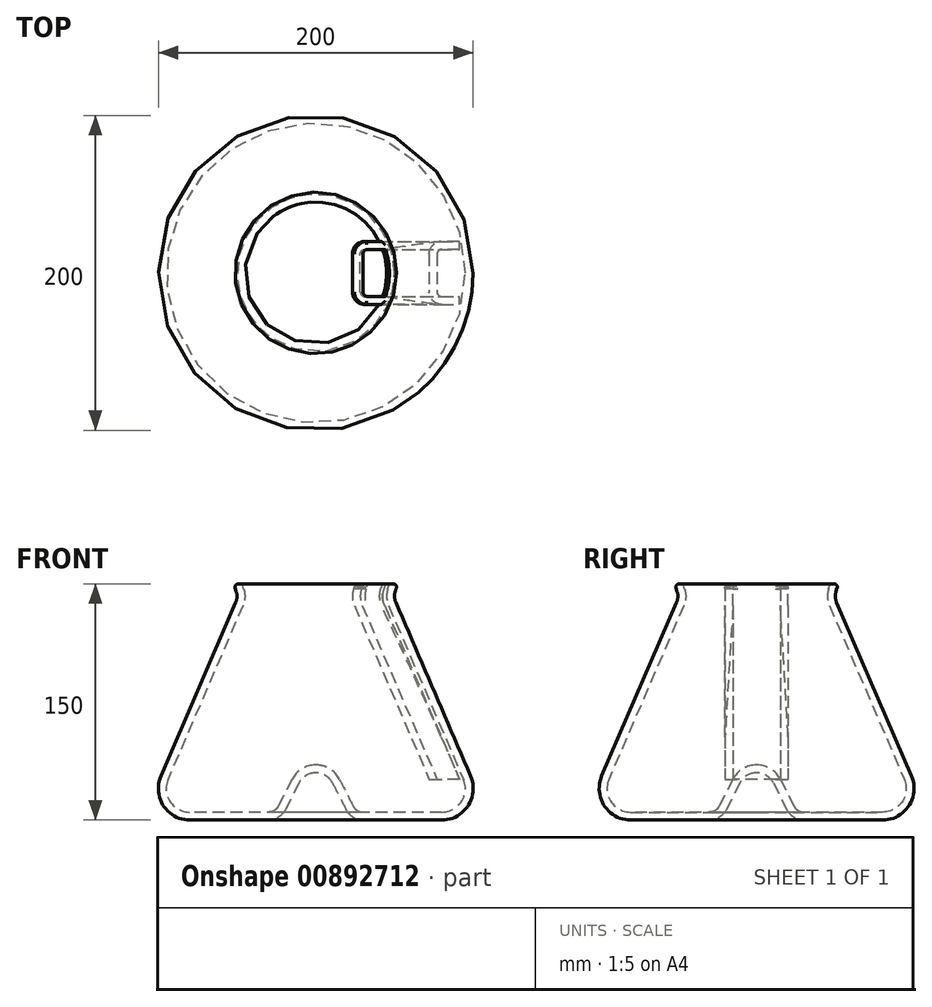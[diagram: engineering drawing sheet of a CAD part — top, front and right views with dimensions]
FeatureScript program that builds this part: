
annotation { "Feature Type Name" : "Feature", "Feature Type Description" : "" }
export const myFeature = defineFeature(function(context is Context, id is Id, definition is map)
    precondition{}
    {
        {
            var Q0;
            Q0=qCreatedBy(makeId("Front.planeOp"),FACE);
            var sketch = newSketch(context, id + "F0", { "sketchPlane" : qUnion([Q0])});
            skArc(sketch, "E0", {"start": v(10.7, 23.45) * mm, "mid": v(6.27, 28.23) * mm, "end": v(0, 30) * mm});
            skLineSegment(sketch, "E1", {"start": v(10.7, 23.45) * mm, "end": v(19.3, 6.55) * mm});
            skArc(sketch, "E2", {"start": v(19.3, 6.55) * mm, "mid": v(23.73, 1.77) * mm, "end": v(30, 0) * mm});
            skLineSegment(sketch, "E3", {"start": v(30, 0) * mm, "end": v(80, 0) * mm});
            skArc(sketch, "E4", {"start": v(80, 0) * mm, "mid": v(96.7, 9) * mm, "end": v(98.37, 27.92) * mm});
            skLineSegment(sketch, "E5", {"start": v(98.37, 27.92) * mm, "end": v(50.82, 138.23) * mm});
            skArc(sketch, "E6", {"start": v(50.48, 145.24) * mm, "mid": v(50.01, 141.7) * mm, "end": v(50.82, 138.23) * mm});
            skLineSegment(sketch, "E7", {"start": v(50.48, 145.24) * mm, "end": v(52, 150) * mm});
            skArc(sketch, "E8.0", {"start": v(15.14, 25.72) * mm, "mid": v(8.88, 32.5) * mm, "end": v(0, 35) * mm});
            skArc(sketch, "E9.1", {"start": v(45.71, 146.76) * mm, "mid": v(45.02, 141.46) * mm, "end": v(46.23, 136.25) * mm});
            skLineSegment(sketch, "E9.2", {"start": v(93.77, 25.94) * mm, "end": v(46.23, 136.25) * mm});
            skArc(sketch, "E9.3", {"start": v(80, 5) * mm, "mid": v(92.53, 11.76) * mm, "end": v(93.77, 25.94) * mm});
            skLineSegment(sketch, "E9.5", {"start": v(15.14, 25.72) * mm, "end": v(23.76, 8.82) * mm});
            skArc(sketch, "E9.6", {"start": v(23.76, 8.82) * mm, "mid": v(26.34, 6.03) * mm, "end": v(30, 5) * mm});
            skLineSegment(sketch, "E9.7", {"start": v(30, 5) * mm, "end": v(80, 5) * mm});
            skLineSegment(sketch, "E10", {"start": v(0, 35) * mm, "end": v(0, 30) * mm});
            skLineSegment(sketch, "E11", {"start": v(45.71, 146.76) * mm, "end": v(46.75, 150) * mm});
            skLineSegment(sketch, "E12", {"start": v(46.75, 150) * mm, "end": v(52, 150) * mm});
            skSolve(sketch);
        }
        {
            var Q0;
            Q0 = qSketchRegion(id + "F0", true);
            var Q1;
            Q1=sQuery(id+"F0.wireOp",EDGE,"E10");
            revolve(context, id + "F1", {"surfaceOperationType" : NewSurfaceOperationType.NEW, "entities" : qUnion([Q0]), "axis" : qUnion([Q1]), "revolveType" : RevolveType.FULL});
        }
        {
            var Q0;
            Q0=makeQuery(id+"F1.opRevolve","SWEPT_EDGE",EDGE,{"disambiguationData":[OSD([sQuery(id+"F0.wireOp",EDGE,"E7"),sQuery(id+"F0.wireOp",EDGE,"DvpDdea2-aXdC-z6Dp-VDlL-zzdlrhbOhZm3")])]});
            fillet(context, id + "F2", {"entities" : qUnion([Q0]), "radius" : 2 * mm, "tangentPropagation" : true, "allowEdgeOverflow" : false});
        }
        {
            var Q0;
            Q0=qCreatedBy(makeId("Top.planeOp"),FACE);
            cPlane(context, id + "F3", {"entities" : qUnion([Q0]), "cplaneType" : CPlaneType.OFFSET, "offset" : 150 * mm, "width" : 150 * mm, "height" : 150 * mm});
        }
        {
            var Q0;
            Q0=qCreatedBy(id+"F3.planeOp",FACE);
            var sketch = newSketch(context, id + "F4", { "sketchPlane" : qUnion([Q0])});
            skCircle(sketch, "E13.0", {"center": v(0, 0) * mm, "radius": 46.75 * mm, "construction": true});
            skLineSegment(sketch, "E14", {"start": v(44.28, 15) * mm, "end": v(33, 15) * mm});
            skLineSegment(sketch, "E15", {"start": v(30, 12) * mm, "end": v(30, -12) * mm});
            skLineSegment(sketch, "E16", {"start": v(33, -15) * mm, "end": v(44.28, -15) * mm});
            skPoint(sketch, "E17.visualSharp", {"position": v(30, 15) * mm});
            skArc(sketch, "E17.filletArc", {"start": v(33, 15) * mm, "mid": v(30.88, 14.12) * mm, "end": v(30, 12) * mm});
            skPoint(sketch, "E18.visualSharp", {"position": v(30, -15) * mm});
            skArc(sketch, "E18.filletArc", {"start": v(30, -12) * mm, "mid": v(30.88, -14.12) * mm, "end": v(33, -15) * mm});
            skPoint(sketch, "E19.visualSharp", {"position": v(27, -18) * mm});
            skPoint(sketch, "E20.visualSharp", {"position": v(27, 18) * mm});
            skLineSegment(sketch, "E21.0", {"start": v(33, -20) * mm, "end": v(44.28, -20) * mm});
            skLineSegment(sketch, "E21.1", {"start": v(44.28, 20) * mm, "end": v(33, 20) * mm});
            skArc(sketch, "E21.2", {"start": v(33, 20) * mm, "mid": v(27.34, 17.66) * mm, "end": v(25, 12) * mm});
            skLineSegment(sketch, "E21.3", {"start": v(25, 12) * mm, "end": v(25, -12) * mm});
            skArc(sketch, "E21.4", {"start": v(25, -12) * mm, "mid": v(27.34, -17.66) * mm, "end": v(33, -20) * mm});
            skLineSegment(sketch, "E22", {"start": v(44.28, -20) * mm, "end": v(44.28, -15) * mm});
            skLineSegment(sketch, "E23", {"start": v(44.28, 15) * mm, "end": v(44.28, 20) * mm});
            skSolve(sketch);
        }
        {
            var Q0;
            Q0=qCreatedBy(makeId("Front.planeOp"),FACE);
            var sketch = newSketch(context, id + "F5", { "sketchPlane" : qUnion([Q0])});
            skLineSegment(sketch, "E24.0", {"start": v(45.71, 146.76) * mm, "end": v(46.75, 150) * mm});
            skArc(sketch, "E25.0", {"start": v(45.71, 146.76) * mm, "mid": v(45.02, 141.46) * mm, "end": v(46.23, 136.25) * mm});
            skLineSegment(sketch, "E26.0", {"start": v(93.77, 25.94) * mm, "end": v(46.23, 136.25) * mm});
            skSolve(sketch);
        }
        {
            var Q0;
            Q0 = qSketchRegion(id + "F4", true);
            var Q1;
            Q1 = qConstructionFilter(qBodyType(qCreatedBy(id + "F5" ,EDGE), BodyType.WIRE), ConstructionObject.NO);
            sweep(context, id + "F6", {"operationType" : NewBodyOperationType.ADD, "profiles" : qUnion([Q0]), "path" : qUnion([Q1]), "keepProfileOrientation" : true});
        }
        {
            var Q0;
            Q0=makeQuery(id+"F6.opSweep","CAP_EDGE",EDGE,{"disambiguationData":[OSD([sQuery(id+"F4.wireOp",EDGE,"E21.1"),sQuery(id+"F5.wireOp",VERTEX,"E24.0.end")])],"isStart":true});
            var Q1;
            Q1=makeQuery(id+"F6.opSweep","CAP_EDGE",EDGE,{"disambiguationData":[OSD([sQuery(id+"F4.wireOp",EDGE,"E21.2"),sQuery(id+"F5.wireOp",VERTEX,"E24.0.end")])],"isStart":true});
            var Q2;
            Q2=makeQuery(id+"F6.opSweep","CAP_EDGE",EDGE,{"disambiguationData":[OSD([sQuery(id+"F4.wireOp",EDGE,"E21.3"),sQuery(id+"F5.wireOp",VERTEX,"E24.0.end")])],"isStart":true});
            var Q3;
            Q3=makeQuery(id+"F6.opSweep","CAP_EDGE",EDGE,{"disambiguationData":[OSD([sQuery(id+"F4.wireOp",EDGE,"E21.4"),sQuery(id+"F5.wireOp",VERTEX,"E24.0.end")])],"isStart":true});
            var Q4;
            Q4=makeQuery(id+"F6.opSweep","CAP_EDGE",EDGE,{"disambiguationData":[OSD([sQuery(id+"F4.wireOp",EDGE,"E21.0"),sQuery(id+"F5.wireOp",VERTEX,"E24.0.end")])],"isStart":true});
            fillet(context, id + "F7", {"entities" : qUnion([Q0, Q1, Q2, Q3, Q4]), "radius" : 2 * mm, "tangentPropagation" : true, "allowEdgeOverflow" : false});
        }
        {
            var Q0;
            {var subQ0=sQuery(id+"F5.wireOp",EDGE,"E24.0");var subQ1=sQuery(id+"F4.wireOp",EDGE,"E21.0");var subQ2=sQuery(id+"F0.wireOp",EDGE,"E11");var subQ4=sQuery(id+"F0.wireOp",EDGE,"E12");Q0=makeQuery(id+"F6.boolean.opBoolean","SPLIT",EDGE,{"disambiguationData":[TD([makeQuery(id+"F6.opSweep","SWEPT_FACE",FACE,{"disambiguationData":[OSD([subQ1,subQ0])]})])],"derivedFrom":makeQuery(id+"F1.opRevolve","SWEPT_EDGE",EDGE,{"disambiguationData":[OSD([subQ2,subQ4])]})});}
            fillet(context, id + "F8", {"entities" : qUnion([Q0]), "radius" : 1 * mm, "tangentPropagation" : true, "allowEdgeOverflow" : false});
        }
    });
